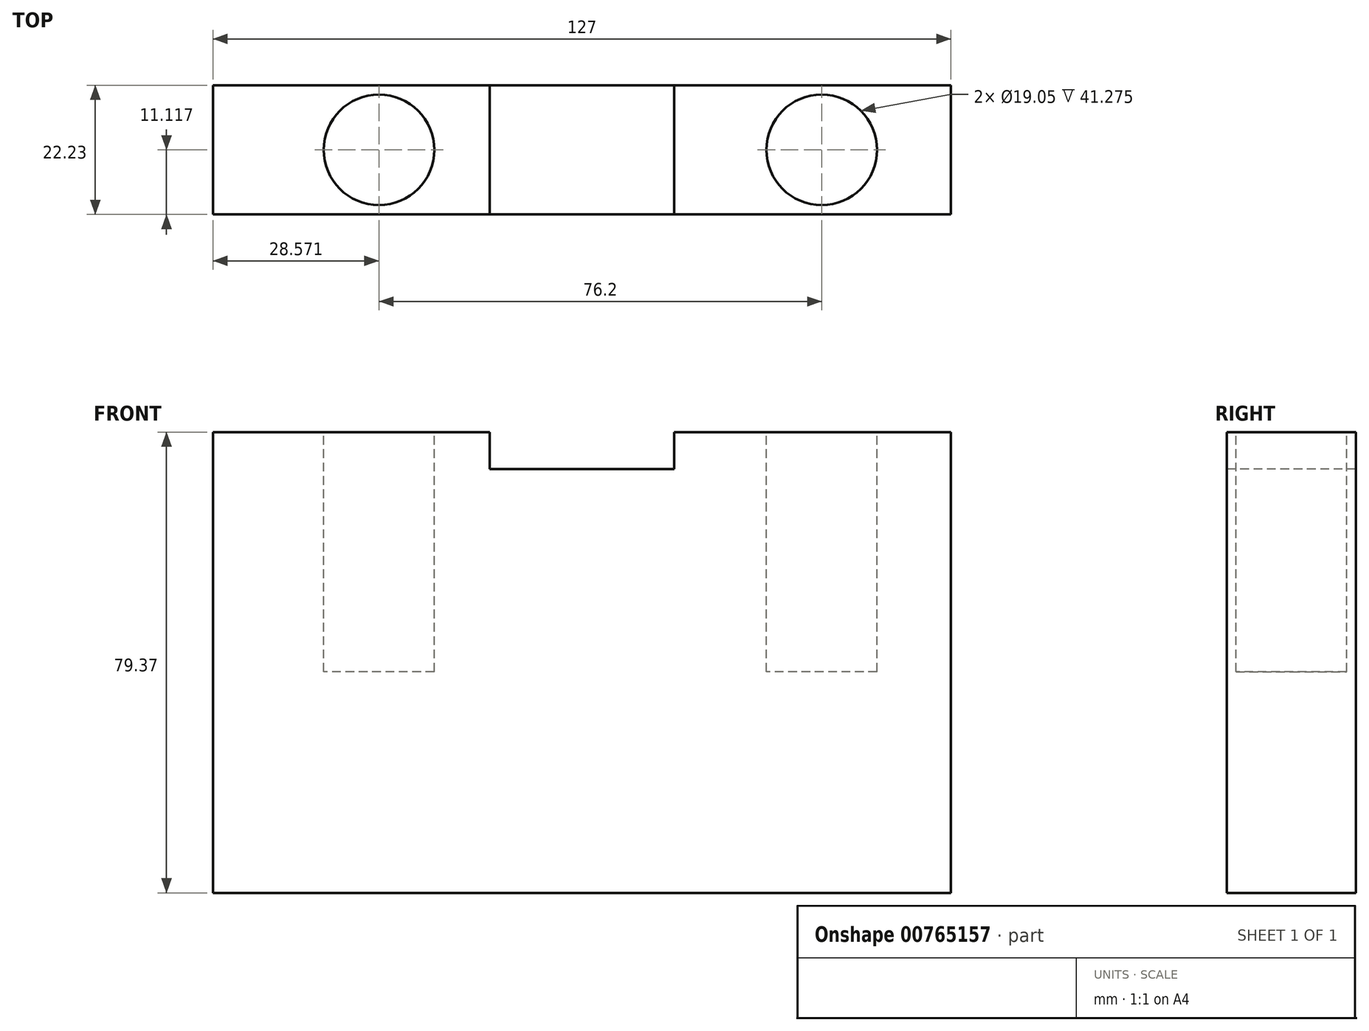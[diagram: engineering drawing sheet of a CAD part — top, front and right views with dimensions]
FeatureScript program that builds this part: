
annotation { "Feature Type Name" : "Feature", "Feature Type Description" : "" }
export const myFeature = defineFeature(function(context is Context, id is Id, definition is map)
    precondition{}
    {
        {
            var Q0;
            Q0=qCreatedBy(makeId("Front.planeOp"),FACE);
            var sketch = newSketch(context, id + "F0", { "sketchPlane" : qUnion([Q0])});
            skLineSegment(sketch, "E0.bottom", {"start": v(-63.2, 30.25) * mm, "end": v(63.8, 30.25) * mm});
            skLineSegment(sketch, "E0.top", {"start": v(-63.2, -42.77) * mm, "end": v(63.8, -42.77) * mm});
            skLineSegment(sketch, "E0.left", {"start": v(-63.2, 30.25) * mm, "end": v(-63.2, -42.77) * mm});
            skLineSegment(sketch, "E0.right", {"start": v(63.8, 30.25) * mm, "end": v(63.8, -42.77) * mm});
            skSolve(sketch);
        }
        {
            var Q0;
            Q0 = qSketchRegion(id + "F0", true);
            extrude(context, id + "F1", {"entities" : qUnion([Q0]), "depth" : 22.22 * mm, "offsetDistance" : 25.4 * mm});
        }
        {
            var Q0;
            Q0=makeQuery(id+"F1.opExtrude","SWEPT_FACE",FACE,{"disambiguationData":[OSD([sQuery(id+"F0.wireOp",EDGE,"E0.bottom")])]});
            var sketch = newSketch(context, id + "F2", { "sketchPlane" : qUnion([Q0])});
            skLineSegment(sketch, "E1.bottom", {"start": v(16.18, 0) * mm, "end": v(63.8, 0) * mm});
            skLineSegment(sketch, "E1.top", {"start": v(16.18, -22.23) * mm, "end": v(63.8, -22.23) * mm});
            skLineSegment(sketch, "E1.left", {"start": v(16.18, 0) * mm, "end": v(16.18, -22.23) * mm});
            skLineSegment(sketch, "E1.right", {"start": v(63.8, 0) * mm, "end": v(63.8, -22.23) * mm});
            skLineSegment(sketch, "E2.bottom", {"start": v(-63.2, 0) * mm, "end": v(-15.57, 0) * mm});
            skLineSegment(sketch, "E2.top", {"start": v(-63.2, -22.23) * mm, "end": v(-15.57, -22.23) * mm});
            skLineSegment(sketch, "E2.left", {"start": v(-63.2, 0) * mm, "end": v(-63.2, -22.23) * mm});
            skLineSegment(sketch, "E2.right", {"start": v(-15.57, 0) * mm, "end": v(-15.57, -22.23) * mm});
            skSolve(sketch);
        }
        {
            var Q0;
            Q0 = qSketchRegion(id + "F2", true);
            extrude(context, id + "F3", {"entities" : qUnion([Q0]), "operationType" : NewBodyOperationType.ADD, "depth" : 6.35 * mm, "offsetDistance" : 25.4 * mm});
        }
        {
            var Q0;
            Q0=makeQuery(id+"F3.opExtrude","CAP_FACE",FACE,{"disambiguationData":[OSD([sQuery(id+"F2.wireOp",EDGE,"E1.bottom"),sQuery(id+"F2.wireOp",EDGE,"E1.top"),sQuery(id+"F2.wireOp",EDGE,"E1.left"),sQuery(id+"F2.wireOp",EDGE,"E1.right")])],"isStart":false});
            var sketch = newSketch(context, id + "F4", { "sketchPlane" : qUnion([Q0])});
            skCircle(sketch, "E3", {"center": v(-34.62, -11.11) * mm, "radius": 9.53 * mm});
            skCircle(sketch, "E4", {"center": v(41.58, -11.11) * mm, "radius": 9.53 * mm});
            skSolve(sketch);
        }
        {
            var Q0;
            Q0 = qSketchRegion(id + "F4", true);
            extrude(context, id + "F5", {"entities" : qUnion([Q0]), "operationType" : NewBodyOperationType.REMOVE, "oppositeDirection" : true, "depth" : 41.27 * mm, "offsetDistance" : 25.4 * mm});
        }
    });
